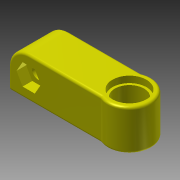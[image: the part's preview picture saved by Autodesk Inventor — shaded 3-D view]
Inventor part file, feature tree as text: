
AUTODESK INVENTOR PART (.ipt)
format: ipt  version: 2013 (Build 170138000, 138)  size: 199,680 bytes
history: native  units: mm
features: extrude x9, sketch x9, chamfer x1, fillet x1
ambient origin geometry x8: Origin, YZ Plane, XZ Plane, XY Plane, X Axis, Y Axis, Z Axis, Center Point
bodies: Solid1 (feature_tree)
feature tree (20):
  extrude  "Extrusion1"  Depth=50.0mm
  extrude  "Extrusion2"  Depth=25.0mm TaperAngle=0.0deg
  extrude  "Extrusion3"  Depth=25.0mm TaperAngle=0.0deg
  extrude  "Extrusion4"  Depth=73.0mm TaperAngle=0.0deg
  extrude  "Extrusion14"  Depth=6.0mm TaperAngle=0.0deg
  extrude  "Extrusion15"  Depth=4.0mm TaperAngle=0.0deg
  extrude  "Extrusion16"  Depth=1.5mm TaperAngle=45.0deg
  chamfer  "Chamfer2"  Distance=10.0mm
  extrude  "Extrusion17"  Depth=10.0mm TaperAngle=0.0deg
  extrude  "Extrusion18"  [1 undecoded]
  fillet  "Fillet1"  [1 undecoded]
  sketch  "Sketch1"  dims[d0=12.5mm d2=50.0mm]
  sketch  "Sketch2"  dims[d3=25.0mm d4=0.0mm d5=25.0mm d6=0.0mm]
  sketch  "Sketch3"  dims[d7=8.1mm d9=25.0mm d10=0.0mm]
  sketch  "Sketch4"  dims[d11=18.1mm d13=73.0mm d14=0.0mm]
  sketch  "Sketch16"  dims[d74=13.1mm d75=6.0mm d76=0.0mm]
  sketch  "Sketch17"  dims[d78=21.1mm d80=4.0mm d81=0.0mm]
  sketch  "Sketch19"  dims[d82=4.0mm d83=0.0mm d84=1.5mm d85=2.0mm d86=45.0deg]
  sketch  "Sketch20"  dims[d87=3.0mm d88=10.0mm d89=0.0mm]
  sketch  "Sketch21"  dims[d90=1.5mm d91=10.0mm d92=0.0mm]
note: 2 required parameter values undecoded (feature->parameter linkage not recoverable at this tier; creation-order binding heuristic only, values carry confidence <= 0.55)
